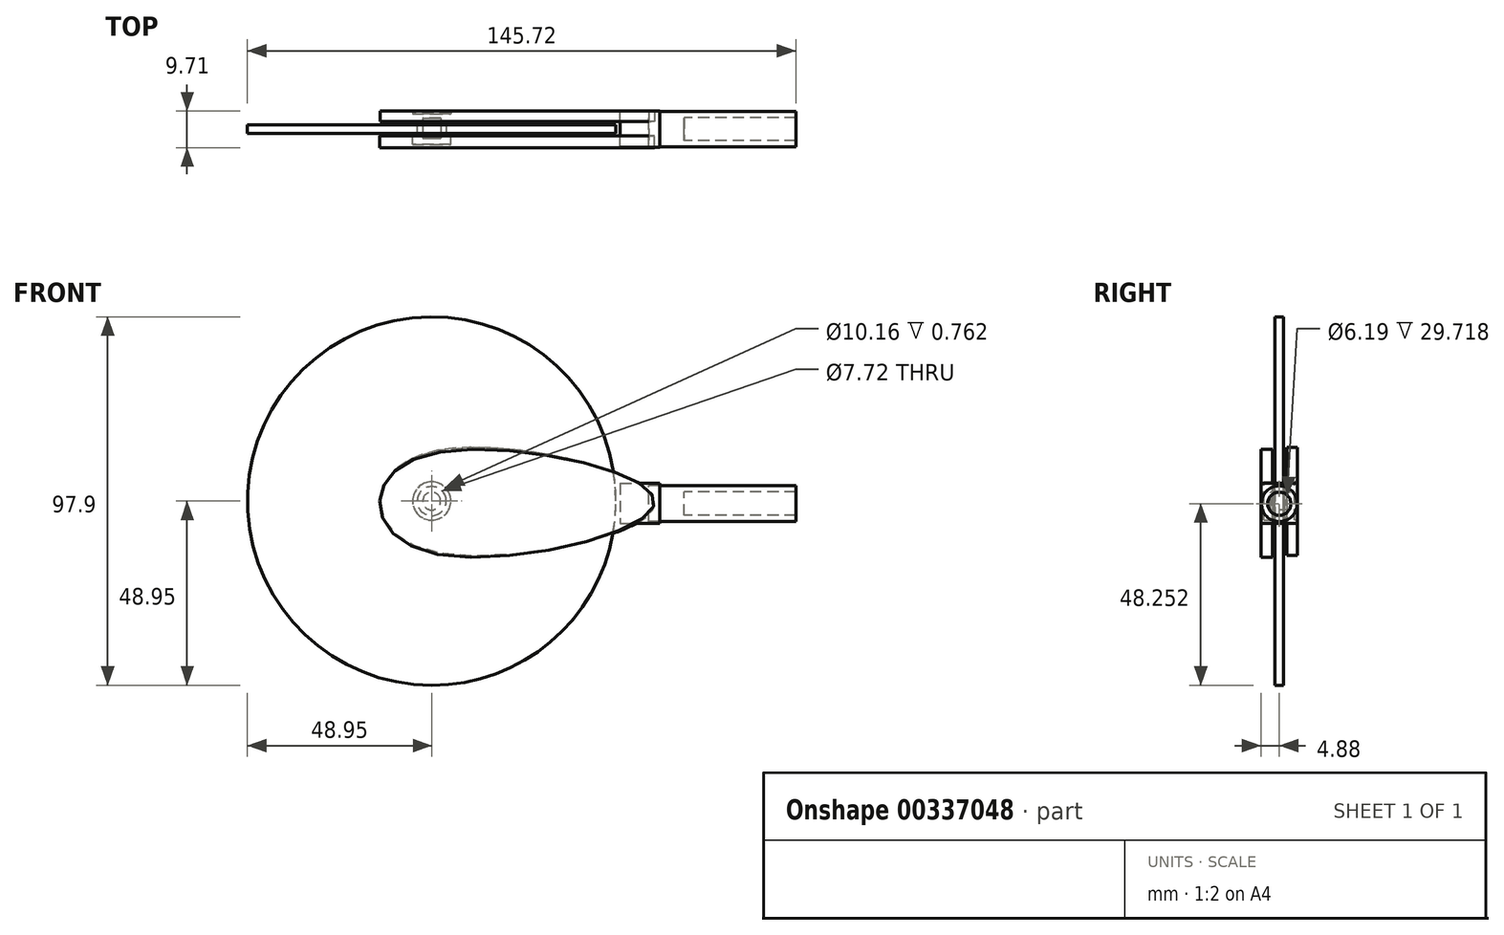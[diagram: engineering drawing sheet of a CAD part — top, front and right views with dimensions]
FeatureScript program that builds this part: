
annotation { "Feature Type Name" : "Feature", "Feature Type Description" : "" }
export const myFeature = defineFeature(function(context is Context, id is Id, definition is map)
    precondition{}
    {
        {
            var Q0;
            Q0=qCreatedBy(makeId("Front.planeOp"),FACE);
            var sketch = newSketch(context, id + "F0", { "sketchPlane" : qUnion([Q0])});
            skCircle(sketch, "E0", {"center": v(0, 0) * mm, "radius": 5.08 * mm});
            skSolve(sketch);
        }
        {
            var Q0;
            Q0 = qSketchRegion(id + "F0", true);
            extrude(context, id + "F1", {"entities" : qUnion([Q0]), "depth" : 4.06 * mm, "hasSecondDirection" : true, "secondDirectionOppositeDirection" : true, "secondDirectionDepth" : 4.06 * mm});
        }
        {
            var Q0;
            Q0=qCreatedBy(makeId("Front.planeOp"),FACE);
            var sketch = newSketch(context, id + "F2", { "sketchPlane" : qUnion([Q0])});
            skCircle(sketch, "E1", {"center": v(0, 0) * mm, "radius": 5.88 * mm});
            skSolve(sketch);
        }
        {
            var Q0;
            Q0 = qSketchRegion(id + "F2", true);
            extrude(context, id + "F3", {"entities" : qUnion([Q0]), "operationType" : NewBodyOperationType.REMOVE, "oppositeDirection" : true, "depth" : 1.32 * mm, "hasSecondDirection" : true, "secondDirectionOppositeDirection" : false, "secondDirectionDepth" : 1.32 * mm});
        }
        {
            var Q0;
            Q0=qCreatedBy(makeId("Front.planeOp"),FACE);
            var sketch = newSketch(context, id + "F4", { "sketchPlane" : qUnion([Q0])});
            skCircle(sketch, "E2", {"center": v(0, 0) * mm, "radius": 2.36 * mm});
            skSolve(sketch);
        }
        {
            var Q0;
            Q0 = qSketchRegion(id + "F4", true);
            extrude(context, id + "F5", {"entities" : qUnion([Q0]), "oppositeDirection" : true, "depth" : 2.95 * mm, "hasSecondDirection" : true, "secondDirectionOppositeDirection" : false, "secondDirectionDepth" : 2.36 * mm});
        }
        {
            var Q0;
            Q0=qCreatedBy(makeId("Front.planeOp"),FACE);
            var sketch = newSketch(context, id + "F6", { "sketchPlane" : qUnion([Q0])});
            skCircle(sketch, "E3", {"center": v(0, 0) * mm, "radius": 3.86 * mm});
            skCircle(sketch, "E4", {"center": v(0, 0) * mm, "radius": 48.95 * mm});
            skSolve(sketch);
        }
        {
            var Q0;
            Q0=makeQuery(id+"F6.imprint","IMPRINT",FACE,{"disambiguationData":[TD([[makeQuery(id+"F6.imprint","IMPRINT",EDGE,{"derivedFrom":sQuery(id+"F6.wireOp",EDGE,"E3")}),-1.0]])]});
            extrude(context, id + "F7", {"entities" : qUnion([Q0]), "oppositeDirection" : true, "depth" : 1.17 * mm, "hasSecondDirection" : true, "secondDirectionOppositeDirection" : false, "secondDirectionDepth" : 1.17 * mm});
        }
        {
            var Q0;
            Q0=qCreatedBy(makeId("Front.planeOp"),FACE);
            var sketch = newSketch(context, id + "F8", { "sketchPlane" : qUnion([Q0])});
            skFitSpline(sketch, "E5", {"points": [v(-13.79, 0) * mm, v(0, 12.6) * mm, v(55.97, 4.2) * mm, v(57.5, -3.43) * mm, v(0, -13.87) * mm, v(-13.79, 0) * mm]});
            skSolve(sketch);
        }
        {
            var Q0;
            Q0=makeQuery(id+"F8.imprint","IMPRINT",FACE,{"disambiguationData":[TD([[makeQuery(id+"F8.imprint","IMPRINT",EDGE,{"derivedFrom":sQuery(id+"F8.wireOp",EDGE,"E5")}),-1.0]])]});
            extrude(context, id + "F9", {"entities" : qUnion([Q0]), "depth" : 4.88 * mm, "hasSecondDirection" : true, "secondDirectionOppositeDirection" : false, "secondDirectionDepth" : 1.78 * mm});
        }
        {
            var Q0;
            Q0=makeQuery(id+"F1.opExtrude","CAP_FACE",FACE,{"disambiguationData":[OSD([sQuery(id+"F0.wireOp",EDGE,"E0")])],"isStart":true});
            var sketch = newSketch(context, id + "F10", { "sketchPlane" : qUnion([Q0])});
            skFitSpline(sketch, "E6", {"points": [v(13.7, -0.7) * mm, v(-0.1, -13.3) * mm, v(-56.06, -4.9) * mm, v(-57.59, 2.73) * mm, v(-0.1, 13.16) * mm, v(13.7, -0.7) * mm]});
            skSolve(sketch);
        }
        {
            var Q0;
            Q0=makeQuery(id+"F10.imprint","IMPRINT",FACE,{"disambiguationData":[TD([[makeQuery(id+"F10.imprint","IMPRINT",EDGE,{"derivedFrom":sQuery(id+"F10.wireOp",EDGE,"E6")}),-1.0]])]});
            extrude(context, id + "F11", {"entities" : qUnion([Q0]), "operationType" : NewBodyOperationType.ADD, "depth" : 0.76 * mm, "hasSecondDirection" : true, "secondDirectionOppositeDirection" : true, "secondDirectionDepth" : 2.03 * mm});
        }
        {
            var Q0;
            Q0=qCreatedBy(makeId("Front.planeOp"),FACE);
            var sketch = newSketch(context, id + "F12", { "sketchPlane" : qUnion([Q0])});
            skLineSegment(sketch, "E7.bottom", {"start": v(50.11, 4.7) * mm, "end": v(60.62, 4.7) * mm});
            skLineSegment(sketch, "E7.top", {"start": v(50.11, -5.9) * mm, "end": v(60.62, -5.9) * mm});
            skLineSegment(sketch, "E7.left", {"start": v(50.11, 4.7) * mm, "end": v(50.11, -5.9) * mm});
            skLineSegment(sketch, "E7.right", {"start": v(60.62, 4.7) * mm, "end": v(60.62, -5.9) * mm});
            skSolve(sketch);
        }
        {
            var Q0;
            Q0=makeQuery(id+"F12.imprint","IMPRINT",FACE,{"disambiguationData":[TD([[makeQuery(id+"F12.imprint","IMPRINT",EDGE,{"derivedFrom":sQuery(id+"F12.wireOp",EDGE,"E7.bottom")}),-1.0]])]});
            extrude(context, id + "F13", {"entities" : qUnion([Q0]), "depth" : 4.85 * mm, "hasSecondDirection" : true, "secondDirectionOppositeDirection" : true, "secondDirectionDepth" : 4.8 * mm});
        }
        {
            var Q0;
            Q0=qCreatedBy(makeId("Right.planeOp"),FACE);
            var sketch = newSketch(context, id + "F14", { "sketchPlane" : qUnion([Q0])});
            skCircle(sketch, "E8", {"center": v(0, -0.7) * mm, "radius": 4.75 * mm});
            skSolve(sketch);
        }
        {
            var Q0;
            Q0 = qSketchRegion(id + "F14", true);
            extrude(context, id + "F15", {"entities" : qUnion([Q0]), "depth" : 96.77 * mm, "hasSecondDirection" : true, "secondDirectionOppositeDirection" : false, "secondDirectionDepth" : 57.66 * mm});
        }
        {
            var Q0;
            Q0=makeQuery(id+"F15.opExtrude","CAP_FACE",FACE,{"disambiguationData":[OSD([sQuery(id+"F14.wireOp",EDGE,"E8")])],"isStart":false});
            var sketch = newSketch(context, id + "F16", { "sketchPlane" : qUnion([Q0])});
            skCircle(sketch, "E9", {"center": v(0, -0.7) * mm, "radius": 3.1 * mm});
            skSolve(sketch);
        }
        {
            var Q0;
            Q0 = qSketchRegion(id + "F16", true);
            extrude(context, id + "F17", {"entities" : qUnion([Q0]), "operationType" : NewBodyOperationType.REMOVE, "depth" : 25.4 * mm, "hasSecondDirection" : true, "secondDirectionOppositeDirection" : true, "secondDirectionDepth" : 29.72 * mm});
        }
    });
